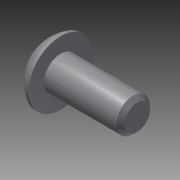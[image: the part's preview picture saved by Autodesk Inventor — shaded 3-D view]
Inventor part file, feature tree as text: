
AUTODESK INVENTOR PART (.ipt)
format: ipt  version: 2015 (Build 190159000, 159)  size: 128,512 bytes
history: native  units: in
note: dims shown in document units (in); Inventor stores cm internally (conversion verified against a paired STEP export)
features: other x3, extrude x1, chamfer x1, imported_body x1, sketch x1
ambient origin geometry x8: Origin, YZ Plane, XZ Plane, XY Plane, X Axis, Y Axis, Z Axis, Center Point
bodies: Body1 (feature_tree)
feature tree (7):
  other  "Bolt 0.375 inch"
  parser-record x1  (decoder bookkeeping rows leaked as tree rows — omitted from the tree; the rows remain in map.json)
  other  "Bolt"
  extrude  "thread length"  Depth=0.375in TaperAngle=0.0deg
  chamfer  "thread chamfer"  Distance=0.02in Angle=45.0deg
  imported_body  "Base1"
  sketch  "Sketch1"  dims[d0=0.164in d1=0.375in d2=0.0in d3=0.02in d4=0.125in d5=45.0deg d7=0.0in d9=0.0in]
